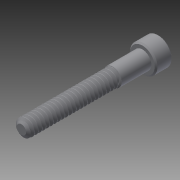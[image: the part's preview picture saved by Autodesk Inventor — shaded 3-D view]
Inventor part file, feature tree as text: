
AUTODESK INVENTOR PART (.ipt)
format: ipt  version: 2015 (Build 190159000, 159)  size: 1,178,624 bytes
history: native  units: in
note: dims shown in document units (in); Inventor stores cm internally (conversion verified against a paired STEP export)
features: chamfer x1, other x1, imported_body x1
ambient origin geometry x8: Origin, YZ Plane, XZ Plane, XY Plane, X Axis, Y Axis, Z Axis, Center Point
bodies: Body1 (feature_tree)
feature tree (3):
  chamfer  "Chamfer1"  [1 undecoded]
  other  "92185A1531"
  imported_body  "Base1"
note: 1 required parameter value undecoded (feature->parameter linkage not recoverable at this tier; creation-order binding heuristic only, values carry confidence <= 0.55)
